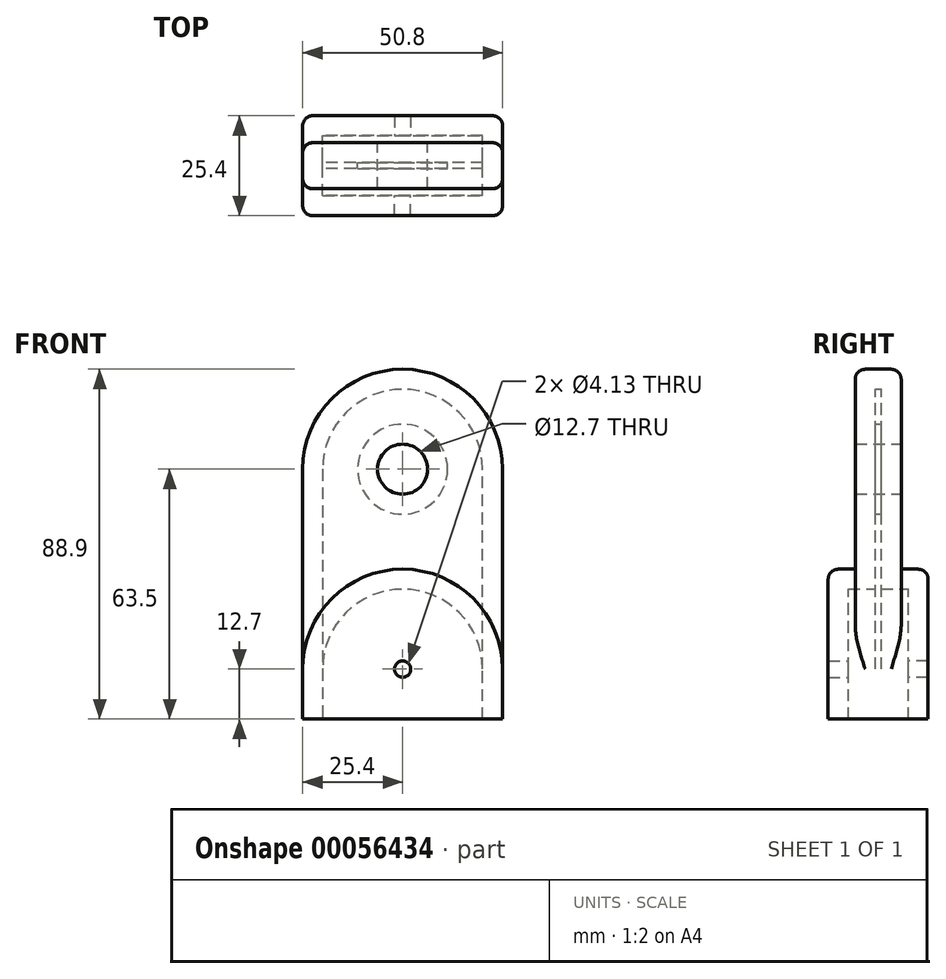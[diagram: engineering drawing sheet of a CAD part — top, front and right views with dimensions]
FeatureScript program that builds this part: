
annotation { "Feature Type Name" : "Feature", "Feature Type Description" : "" }
export const myFeature = defineFeature(function(context is Context, id is Id, definition is map)
    precondition{}
    {
        {
            var Q0;
            Q0=qCreatedBy(makeId("Front.planeOp"),FACE);
            var sketch = newSketch(context, id + "F0", { "sketchPlane" : qUnion([Q0])});
            skCircle(sketch, "E0", {"center": v(0, 0) * mm, "radius": 25.4 * mm});
            skLineSegment(sketch, "E1.bottom", {"start": v(-25.4, 0) * mm, "end": v(25.4, 0) * mm});
            skLineSegment(sketch, "E1.top", {"start": v(-25.4, -63.5) * mm, "end": v(25.4, -63.5) * mm});
            skLineSegment(sketch, "E1.left", {"start": v(-25.4, 0) * mm, "end": v(-25.4, -63.5) * mm});
            skLineSegment(sketch, "E1.right", {"start": v(25.4, 0) * mm, "end": v(25.4, -63.5) * mm});
            skCircle(sketch, "E2", {"center": v(0, 0) * mm, "radius": 6.35 * mm});
            skLineSegment(sketch, "E3", {"start": v(-25.4, -25.4) * mm, "end": v(25.4, -25.4) * mm});
            skCircle(sketch, "E4", {"center": v(0, -50.8) * mm, "radius": 25.4 * mm});
            skSolve(sketch);
        }
        {
            var Q0;
            {var subQ0=sQuery(id+"F0.wireOp",EDGE,"E1.bottom");var subQ4=sQuery(id+"F0.wireOp",EDGE,"E2");var subQ5=makeQuery(id+"F0.imprint","INTERSECT",VERTEX,{"disambiguationData":[OD(0.0)],"derivedFrom":[subQ0,subQ4]});Q0=makeQuery(id+"F0.imprint","IMPRINT",FACE,{"disambiguationData":[TD([[makeQuery(id+"F0.imprint","IMPRINT",EDGE,{"disambiguationData":[TD([[subQ5,1.0]])],"derivedFrom":subQ4}),-1.0]])]});}
            var Q1;
            {var subQ0=sQuery(id+"F0.wireOp",EDGE,"E1.bottom");var subQ3=sQuery(id+"F0.wireOp",EDGE,"E2");var subQ5=makeQuery(id+"F0.imprint","INTERSECT",VERTEX,{"disambiguationData":[OD(0.0)],"derivedFrom":[subQ0,subQ3]});Q1=makeQuery(id+"F0.imprint","IMPRINT",FACE,{"disambiguationData":[TD([[makeQuery(id+"F0.imprint","IMPRINT",EDGE,{"disambiguationData":[TD([[subQ5,-1.0]])],"derivedFrom":subQ3}),-1.0]])]});}
            var Q2;
            {var subQ0=sQuery(id+"F0.wireOp",EDGE,"E1.left");var subQ3=sQuery(id+"F0.wireOp",EDGE,"E3");var subQ5=makeQuery(id+"F0.imprint","INTERSECT",VERTEX,{"derivedFrom":[subQ0,subQ3]});Q2=makeQuery(id+"F0.imprint","IMPRINT",FACE,{"disambiguationData":[TD([[makeQuery(id+"F0.imprint","IMPRINT",EDGE,{"disambiguationData":[TD([[subQ5,1.0]])],"derivedFrom":subQ0}),1.0]])]});}
            var Q3;
            {var subQ0=sQuery(id+"F0.wireOp",EDGE,"E1.right");var subQ3=sQuery(id+"F0.wireOp",EDGE,"E3");var subQ5=makeQuery(id+"F0.imprint","INTERSECT",VERTEX,{"derivedFrom":[subQ0,subQ3]});Q3=makeQuery(id+"F0.imprint","IMPRINT",FACE,{"disambiguationData":[TD([[makeQuery(id+"F0.imprint","IMPRINT",EDGE,{"disambiguationData":[TD([[subQ5,1.0]])],"derivedFrom":subQ0}),-1.0]])]});}
            var Q4;
            {var subQ0=sQuery(id+"F0.wireOp",EDGE,"E3");var subQ1=sQuery(id+"F0.wireOp",EDGE,"E1.right");var subQ2=makeQuery(id+"F0.imprint","INTERSECT",VERTEX,{"derivedFrom":[subQ1,subQ0]});Q4=makeQuery(id+"F0.imprint","IMPRINT",FACE,{"disambiguationData":[TD([[makeQuery(id+"F0.imprint","IMPRINT",EDGE,{"disambiguationData":[TD([[subQ2,-1.0]])],"derivedFrom":subQ1}),-1.0]])]});}
            var Q5;
            {var subQ0=sQuery(id+"F0.wireOp",EDGE,"E3");var subQ1=sQuery(id+"F0.wireOp",EDGE,"E1.left");var subQ2=makeQuery(id+"F0.imprint","INTERSECT",VERTEX,{"derivedFrom":[subQ1,subQ0]});Q5=makeQuery(id+"F0.imprint","IMPRINT",FACE,{"disambiguationData":[TD([[makeQuery(id+"F0.imprint","IMPRINT",EDGE,{"disambiguationData":[TD([[subQ2,-1.0]])],"derivedFrom":subQ1}),1.0]])]});}
            extrude(context, id + "F1", {"entities" : qUnion([Q0, Q1, Q2, Q3, Q4, Q5]), "endBound" : BoundingType.SYMMETRIC, "depth" : 11.68 * mm});
        }
        {
            var Q0;
            {var subQ0=sQuery(id+"F0.wireOp",EDGE,"E1.left");var subQ1=sQuery(id+"F0.wireOp",EDGE,"E1.top");var subQ2=makeQuery(id+"F0.imprint","INTERSECT",VERTEX,{"derivedFrom":[subQ1,subQ0]});Q0=makeQuery(id+"F0.imprint","IMPRINT",FACE,{"disambiguationData":[TD([[makeQuery(id+"F0.imprint","IMPRINT",EDGE,{"disambiguationData":[TD([[subQ2,-1.0]])],"derivedFrom":subQ1}),1.0]])]});}
            var Q1;
            {var subQ0=sQuery(id+"F0.wireOp",EDGE,"E4");var subQ1=sQuery(id+"F0.wireOp",EDGE,"E1.top");var subQ2=makeQuery(id+"F0.imprint","INTERSECT",VERTEX,{"disambiguationData":[OD(0.0)],"derivedFrom":[subQ1,subQ0]});Q1=makeQuery(id+"F0.imprint","IMPRINT",FACE,{"disambiguationData":[TD([[makeQuery(id+"F0.imprint","IMPRINT",EDGE,{"disambiguationData":[TD([[subQ2,-1.0]])],"derivedFrom":subQ1}),1.0]])]});}
            var Q2;
            {var subQ0=sQuery(id+"F0.wireOp",EDGE,"E1.right");var subQ1=sQuery(id+"F0.wireOp",EDGE,"E1.top");var subQ2=makeQuery(id+"F0.imprint","INTERSECT",VERTEX,{"derivedFrom":[subQ1,subQ0]});Q2=makeQuery(id+"F0.imprint","IMPRINT",FACE,{"disambiguationData":[TD([[makeQuery(id+"F0.imprint","IMPRINT",EDGE,{"disambiguationData":[TD([[subQ2,1.0]])],"derivedFrom":subQ1}),1.0]])]});}
            extrude(context, id + "F2", {"entities" : qUnion([Q0, Q1, Q2]), "operationType" : NewBodyOperationType.ADD, "endBound" : BoundingType.SYMMETRIC, "depth" : 25.4 * mm});
        }
        {
            var Q0;
            Q0=makeQuery(id+"F1.opExtrude","CAP_EDGE",EDGE,{"disambiguationData":[OSD([sQuery(id+"F0.wireOp",EDGE,"E0")])],"isStart":false});
            var Q1;
            Q1=makeQuery(id+"F1.opExtrude","CAP_EDGE",EDGE,{"disambiguationData":[OSD([sQuery(id+"F0.wireOp",EDGE,"E0")])],"isStart":true});
            var Q2;
            Q2=makeQuery(id+"F2.opExtrude","CAP_EDGE",EDGE,{"disambiguationData":[OSD([sQuery(id+"F0.wireOp",EDGE,"E4")])],"isStart":false});
            var Q3;
            Q3=makeQuery(id+"F2.opExtrude","CAP_EDGE",EDGE,{"disambiguationData":[OSD([sQuery(id+"F0.wireOp",EDGE,"E4")])],"isStart":true});
            fillet(context, id + "F3", {"entities" : qUnion([Q0, Q1, Q2, Q3]), "radius" : 2.54 * mm, "tangentPropagation" : true, "allowEdgeOverflow" : false});
        }
        {
            var Q0;
            Q0=makeQuery(id+"F2.opExtrude","SWEPT_FACE",FACE,{"disambiguationData":[OSD([sQuery(id+"F0.wireOp",EDGE,"E1.top")])]});
            shell(context, id + "F4", {"entities" : qUnion([Q0]), "thickness" : 5.08 * mm});
        }
        {
            var Q0;
            Q0=sQuery(id+"F0.wireOp",VERTEX,"E4.center");
            var Q1;
            Q1=makeQuery(id+"F1.opExtrude","SWEPT_BODY",BODY,{"disambiguationData":[OSD([sQuery(id+"F0.wireOp",EDGE,"E0"),sQuery(id+"F0.wireOp",EDGE,"E1.left"),sQuery(id+"F0.wireOp",EDGE,"E1.right"),sQuery(id+"F0.wireOp",EDGE,"E2"),sQuery(id+"F0.wireOp",EDGE,"E4")])]});
            hole(context, id + "F5", {"style" : HoleStyle.SIMPLE, "holeDiameter" : 4.13 * mm, "endStyle" : HoleEndStyle.THROUGH, "locations" : qUnion([Q0]), "scope" : qUnion([Q1])});
        }
        {
            var Q0;
            Q0=sQuery(id+"F0.wireOp",VERTEX,"E4.center");
            var Q1;
            Q1=makeQuery(id+"F1.opExtrude","SWEPT_BODY",BODY,{"disambiguationData":[OSD([sQuery(id+"F0.wireOp",EDGE,"E0"),sQuery(id+"F0.wireOp",EDGE,"E1.left"),sQuery(id+"F0.wireOp",EDGE,"E1.right"),sQuery(id+"F0.wireOp",EDGE,"E2"),sQuery(id+"F0.wireOp",EDGE,"E4")])]});
            hole(context, id + "F6", {"style" : HoleStyle.SIMPLE, "holeDiameter" : 4.13 * mm, "endStyle" : HoleEndStyle.THROUGH, "oppositeDirection" : true, "locations" : qUnion([Q0]), "scope" : qUnion([Q1])});
        }
    });
